# Revit family: Bath-Drop_In-KOHLER-Memoirs-K-1169
name_source: partatom
category: Plumbing Fixtures
revit_build: Autodesk Revit 2015 (Build: 20140606_1530(x64)
units: mm (PartAtom-declared; Revit-internal decimal feet)

## types (5) — shared parameters
ADA Compliant = No
Assembly Code = D2010500
CW Connection = No
Cold Water Inlet = Cold Water Inlet
Date Modified = 03/04/2019
Default Elevation = 0"
Description = 66 inch x 42 inch drop-in bath
Drain Included = No
HW Connection = No
Height = 22"
Hot Water Inlet = Hot Water Inlet
Length = 66"
Manufacturer = KOHLER Co.
MasterFormat 1995 = 15410
MasterFormat 2004 = 22.41.19
Material = Acrylic
Product Documentation Link = https://www.us.kohler.com
Product Name = Memoirs
Product Page URL = http://www.us.kohler.com
URL = https://www.us.kohler.com
Vent Connection = No
Waste Connection = Yes
Waste Water Outlet = Waste Water Outlet
WaterSense Certified = No
Width = 42"

## per-type parameters (varying)
| type | Finish | Model | Type |
| 0-White | Kohler-Acrylic-0-White | K-1169-0 | 1 |
| 96-Biscuit | Kohler-Acrylic-96-Biscuit | K-1169-96 | 2 |
| 47-Almond | Kohler-Acrylic-47-Almond | K-1169-47 | 3 |
| NY-Dune | Kohler-Acrylic-NY-Dune | K-1169-NY | 4 |
| G9-Sandbar | Kohler-Acrylic-G9-Sandbar | K-1169-G9 | 5 |

## geometry (parser evidence)
native form markers: Sweep x6
no freeform markers — native parametric forms only
